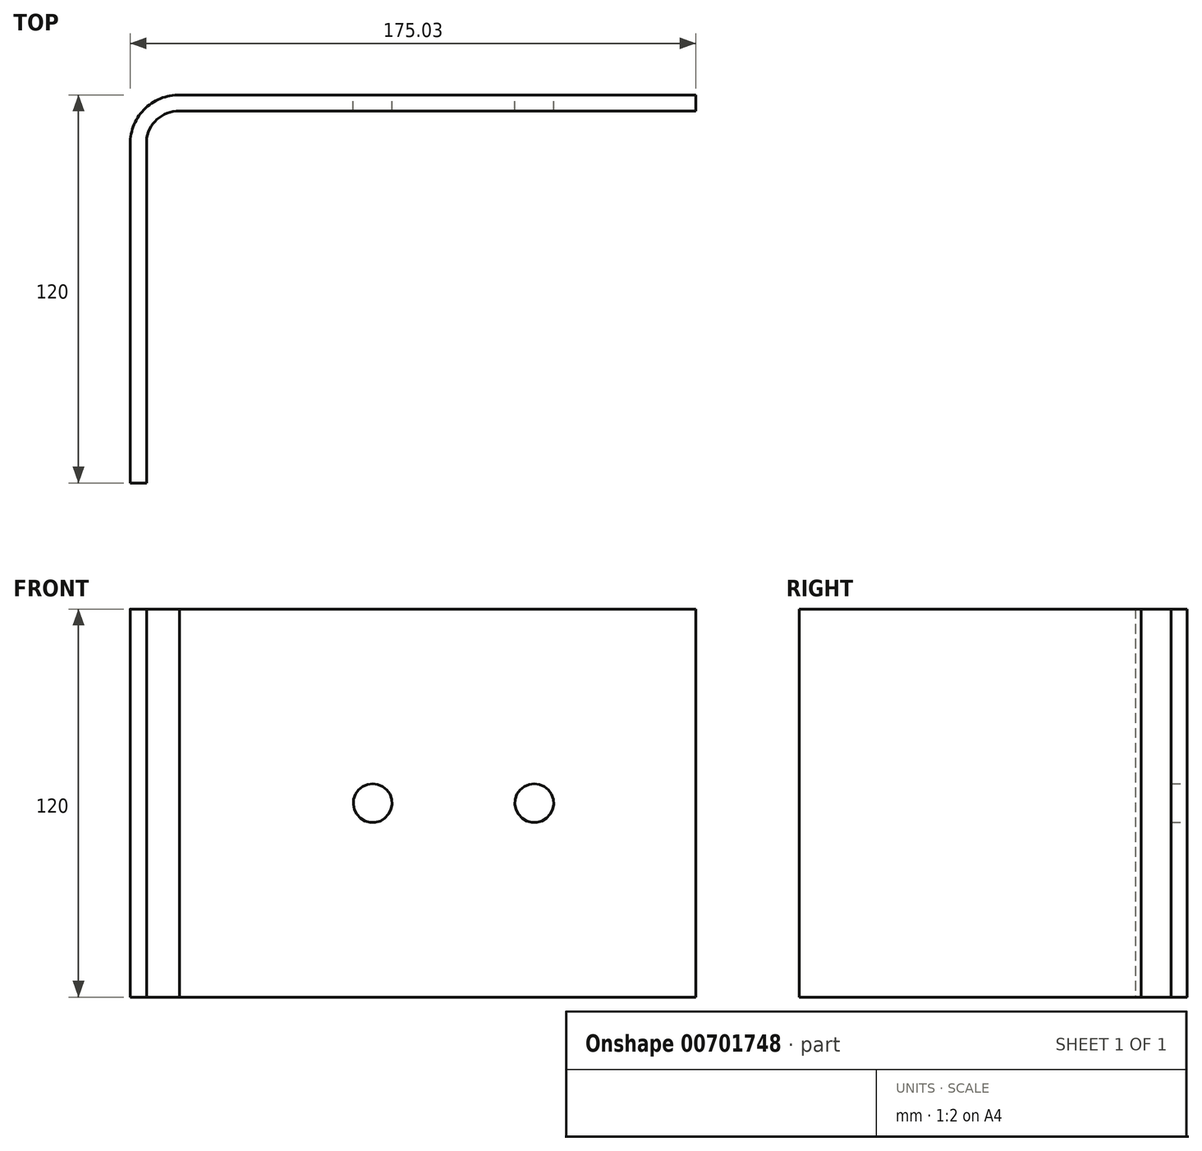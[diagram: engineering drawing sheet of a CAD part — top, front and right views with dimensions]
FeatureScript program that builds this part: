
annotation { "Feature Type Name" : "Feature", "Feature Type Description" : "" }
export const myFeature = defineFeature(function(context is Context, id is Id, definition is map)
    precondition{}
    {
        {
            var Q0;
            Q0=qCreatedBy(makeId("Top.planeOp"),FACE);
            var sketch = newSketch(context, id + "F0", { "sketchPlane" : qUnion([Q0])});
            skArc(sketch, "E0", {"start": v(-28.38, 31.77) * mm, "mid": v(-28.38, 31.77) * mm, "end": v(-28.38, 31.77) * mm});
            skLineSegment(sketch, "E1", {"start": v(-39.18, 36.77) * mm, "end": v(120.46, 36.77) * mm});
            skLineSegment(sketch, "E2", {"start": v(-54.54, 20.82) * mm, "end": v(-54.54, -83.23) * mm});
            skArc(sketch, "E3.0", {"start": v(-39.34, 31.77) * mm, "mid": v(-46.28, 29.18) * mm, "end": v(-49.54, 22.53) * mm});
            skLineSegment(sketch, "E4", {"start": v(-49.54, 22.53) * mm, "end": v(-49.54, -83.23) * mm});
            skLineSegment(sketch, "E5", {"start": v(-49.54, -83.23) * mm, "end": v(-54.54, -83.23) * mm});
            skLineSegment(sketch, "E6", {"start": v(-39.34, 31.77) * mm, "end": v(120.46, 31.77) * mm});
            skLineSegment(sketch, "E7", {"start": v(120.46, 31.77) * mm, "end": v(120.46, 36.77) * mm});
            skArc(sketch, "E8.trimOffspring", {"start": v(-49.54, 10.56) * mm, "mid": v(-49.54, 10.56) * mm, "end": v(-49.54, 10.56) * mm});
            skArc(sketch, "E9.trimOffspring", {"start": v(-39.18, 36.77) * mm, "mid": v(-50.37, 32.17) * mm, "end": v(-54.54, 20.82) * mm});
            skSolve(sketch);
        }
        {
            var Q0;
            Q0 = qSketchRegion(id + "F0", true);
            extrude(context, id + "F1", {"entities" : qUnion([Q0]), "depth" : 120 * mm, "offsetDistance" : 25 * mm});
        }
        {
            var Q0;
            Q0=makeQuery(id+"F1.opExtrude","SWEPT_FACE",FACE,{"disambiguationData":[OSD([sQuery(id+"F0.wireOp",EDGE,"E1")])]});
            var sketch = newSketch(context, id + "F2", { "sketchPlane" : qUnion([Q0])});
            skCircle(sketch, "E10", {"center": v(-70.46, 60) * mm, "radius": 6 * mm});
            skCircle(sketch, "E11", {"center": v(-20.46, 60) * mm, "radius": 6 * mm});
            skSolve(sketch);
        }
        {
            var Q0;
            Q0=makeQuery(id+"F2.imprint","IMPRINT",FACE,{"disambiguationData":[TD([[makeQuery(id+"F2.imprint","IMPRINT",EDGE,{"derivedFrom":sQuery(id+"F2.wireOp",EDGE,"E10")}),1.0]])]});
            var Q1;
            Q1=makeQuery(id+"F2.imprint","IMPRINT",FACE,{"disambiguationData":[TD([[makeQuery(id+"F2.imprint","IMPRINT",EDGE,{"derivedFrom":sQuery(id+"F2.wireOp",EDGE,"E11")}),1.0]])]});
            var Q2;
            Q2=sQuery(id+"F2.wireOp",EDGE,"E11");
            var Q3;
            Q3=sQuery(id+"F2.wireOp",EDGE,"E10");
            extrude(context, id + "F3", {"entities" : qUnion([Q0, Q1]), "operationType" : NewBodyOperationType.REMOVE, "surfaceEntities" : qUnion([Q2, Q3]), "oppositeDirection" : true, "depth" : 5 * mm, "offsetDistance" : 25 * mm});
        }
    });
